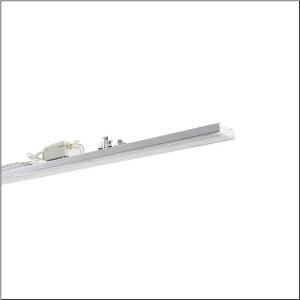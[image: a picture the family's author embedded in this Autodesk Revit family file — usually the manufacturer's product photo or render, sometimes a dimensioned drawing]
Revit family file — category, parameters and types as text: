
# Revit family: licross_r__21_recessed_ho_52tl12dn4fxm_8daa
name_source: partatom
category: Lighting Fixtures
units: mm (PartAtom-declared; Revit-internal decimal feet)

## family parameters
Cut with Voids When Loaded = No
Host = Face
Light Source = No
Part Type = Normal
Room Calculation Point = No
Round Connector Dimension = Use Diameter
Shared = No

## types (1)
- --- (1 x LED, 15000 lm, 84.6 W, 4000K)
    Apparent Load = 85 VA
    CIE Flux Codes = 69 91 98 100 100
    Color Rendering = 80
    Color Temperature = 4000K
    Default Elevation = 1800 mm
    Description = Licross® 21 Recessed HO, luminaire insert, of sheet steel, galvanised, coil coated, white, length: 1.500mm, width: 66mm, height: 67mm, LED rated luminous flux: 15.000lm, light colour: 840, control gear: DALI 2, with plug, 5-pole, with phase selection, mains connection: 220..240V, AC, 50/60Hz, rated input power: 85W, halogen-free wiring, primary optical cover: cover, of PMMA, light emission: direct distribution, primary light characteristic: symmetric, protection rating (complete): IP40, insulation class (complete): insulation class I (protective earthing), certification: CE, ENEC, VDE, UKCA, protection symbol: D if used in an environment without relevant dust loads with corresponding accessories, impact resistance: IK06, permissible ambient temperature for indoor applications: -25..+30°C, corresponds to IFS (International Featured Standards) requirements for safety and quality in the food industry, reducing of maximum allowable ambient temperature of 5°C with ceiling mounting, LABS conformity tested according to VDMA 24364:2018-05, packaging unit: 1 piece
    Height = 58 mm
    Lamp = 1 x LED
    Lamp Light Flux = 15000 lm
    Lamp Power = 84.6 W
    Lamp count = 1
    Length = 1500 mm
    Luminous efficacy = 177 lm/W
    Manufacturer = Siteco
    ModVariant = No
    Model = 52TL12DN4FXM
    Mounting Place = Ceiling
    Mounting Type = Pendant
    Number of Poles = 1
    OnlyDefault = Yes
    Power Factor = 1
    Product Name = Licross® 21 Recessed HO
    Product group = luminaire insert
    ProductGroupID = 901
    Protection Class = Protection class I
    Protection Degree = IP 40
    RLX_Detail_Level = 1
    RLX_Emergency_Light_Flux = 0 lm
    RLX_Emergency_Type = 0
    RLX_Emergency_Type_DB = No
    RlxData = <blob elided: 24673 chars, md5=0d00e465>
    Socket = socket
    Standby Power = 0 W
    System Light Flux = 15000 lm
    System Power = 85 W
    Type Comments = factory setting: luminous flux: 100 % | dim-lin: 254 | 484 mA
    Type Image = l_1296930.jpg
    URL = http://relux.com
    VarID = @adj_046597
    Voltage = 0 V
    Weight = 0.00 kg
    Width = 66 mm

## geometry (parser evidence)
native form markers: Blend x4, Sweep x14
no freeform markers — native parametric forms only
